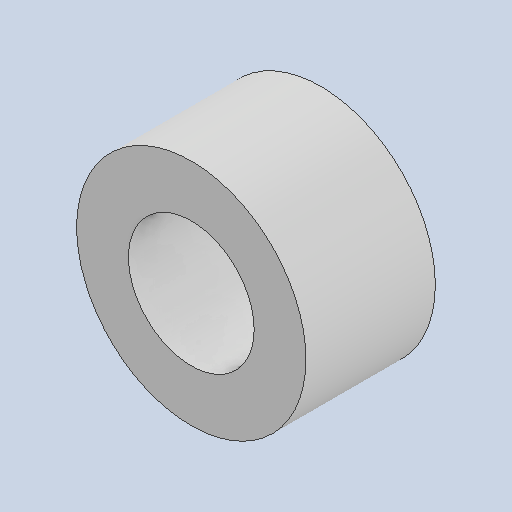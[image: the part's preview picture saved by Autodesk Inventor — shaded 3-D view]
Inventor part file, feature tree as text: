
AUTODESK INVENTOR PART (.ipt)
format: ipt  version: 2024 (Build 280153000, 153)  size: 95,744 bytes
history: native  units: in
note: dims shown in document units (in); Inventor stores cm internally (conversion verified against a paired STEP export)
features: other x3, sketch x1
ambient origin geometry x8: Origin, YZ Plane, XZ Plane, XY Plane, X Axis, Y Axis, Z Axis, Center Point
bodies: Solid1 (feature_tree)
feature tree (4):
  other  "Part2.ipt"
  other  "Solid1::Part2.ipt"
  other  "TaggingFeature1"
  sketch  "Sketch1"  dims[d0=0.3937in]
